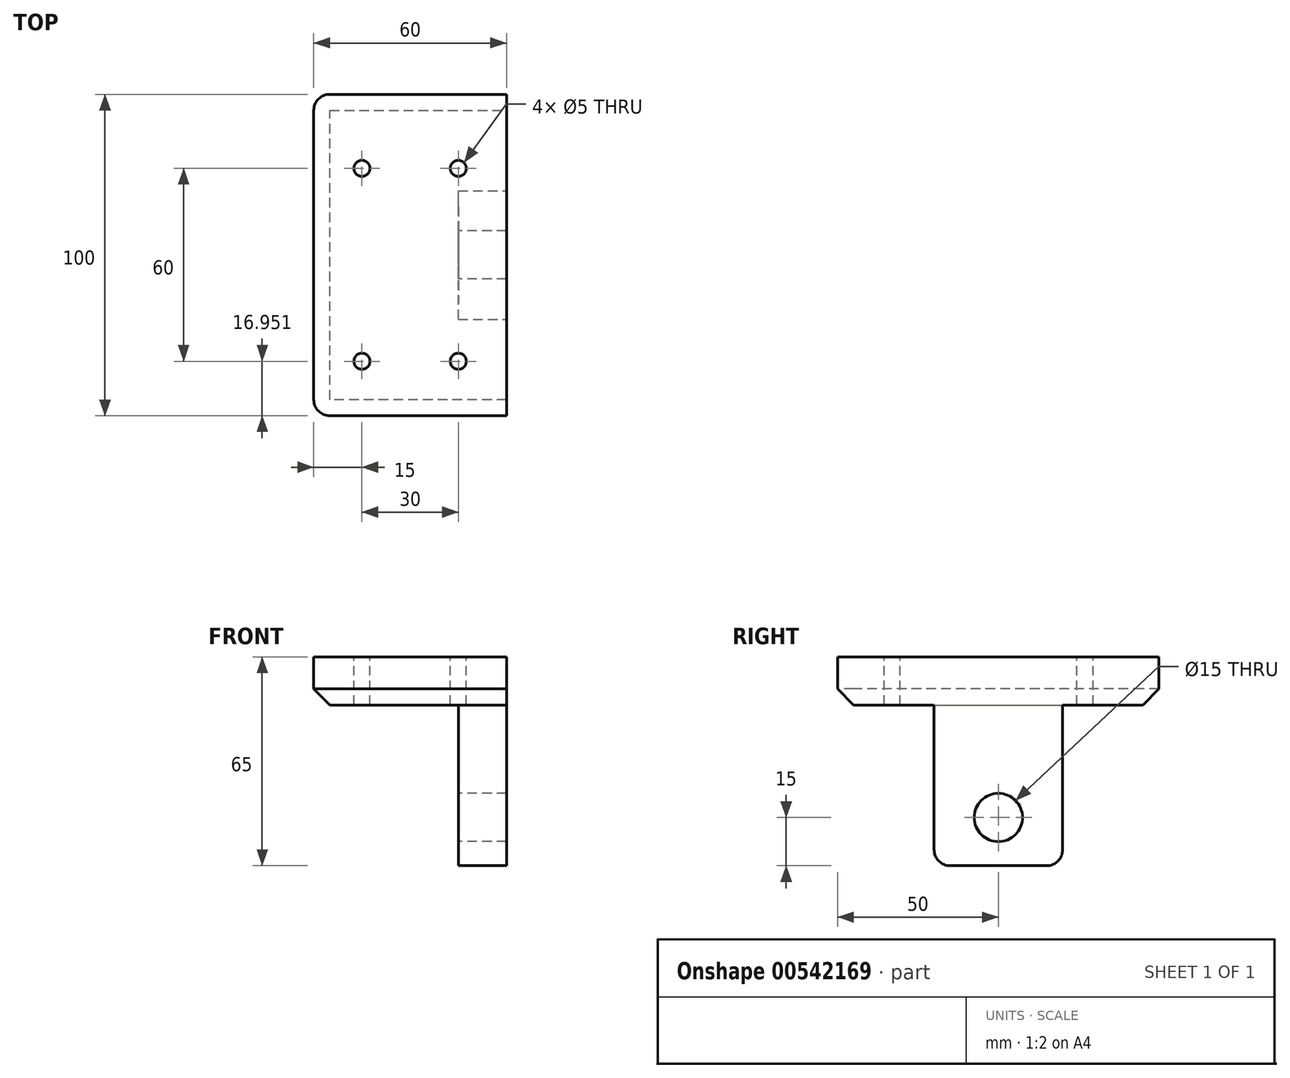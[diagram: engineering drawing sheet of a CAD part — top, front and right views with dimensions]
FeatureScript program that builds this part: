
annotation { "Feature Type Name" : "Feature", "Feature Type Description" : "" }
export const myFeature = defineFeature(function(context is Context, id is Id, definition is map)
    precondition{}
    {
        {
            var Q0;
            Q0=qCreatedBy(makeId("Top.planeOp"),FACE);
            var sketch = newSketch(context, id + "F0", { "sketchPlane" : qUnion([Q0])});
            skLineSegment(sketch, "E0.bottom", {"start": v(5, 0) * mm, "end": v(60, 0) * mm});
            skLineSegment(sketch, "E0.top", {"start": v(5, 100) * mm, "end": v(60, 100) * mm});
            skLineSegment(sketch, "E0.left", {"start": v(0, 5) * mm, "end": v(0, 95) * mm});
            skLineSegment(sketch, "E0.right", {"start": v(60, 0) * mm, "end": v(60, 100) * mm});
            skPoint(sketch, "E1.visualSharp", {"position": v(0, 100) * mm});
            skArc(sketch, "E1.filletArc", {"start": v(5, 100) * mm, "mid": v(1.46, 98.54) * mm, "end": v(0, 95) * mm});
            skPoint(sketch, "E2.visualSharp", {"position": v(0, 0) * mm});
            skArc(sketch, "E2.filletArc", {"start": v(0, 5) * mm, "mid": v(1.46, 1.46) * mm, "end": v(5, 0) * mm});
            skSolve(sketch);
        }
        {
            var Q0;
            Q0=makeQuery(id+"F0.imprint","IMPRINT",FACE,{"disambiguationData":[TD([[makeQuery(id+"F0.imprint","IMPRINT",EDGE,{"derivedFrom":sQuery(id+"F0.wireOp",EDGE,"E0.bottom")}),1.0]])]});
            extrude(context, id + "F1", {"entities" : qUnion([Q0]), "oppositeDirection" : true, "depth" : 15 * mm, "offsetDistance" : 25 * mm});
        }
        {
            var Q0;
            Q0=makeQuery(id+"F1.opExtrude","SWEPT_FACE",FACE,{"disambiguationData":[OSD([sQuery(id+"F0.wireOp",EDGE,"E0.right")])]});
            var sketch = newSketch(context, id + "F2", { "sketchPlane" : qUnion([Q0])});
            skLineSegment(sketch, "E3.bottom", {"start": v(70, -15) * mm, "end": v(30, -15) * mm});
            skLineSegment(sketch, "E3.top", {"start": v(70, -65) * mm, "end": v(30, -65) * mm});
            skLineSegment(sketch, "E3.left", {"start": v(70, -15) * mm, "end": v(70, -65) * mm});
            skLineSegment(sketch, "E3.right", {"start": v(30, -15) * mm, "end": v(30, -65) * mm});
            skSolve(sketch);
        }
        {
            var Q0;
            Q0=makeQuery(id+"F2.imprint","IMPRINT",FACE,{"disambiguationData":[TD([[makeQuery(id+"F2.imprint","IMPRINT",EDGE,{"derivedFrom":sQuery(id+"F2.wireOp",EDGE,"E3.bottom")}),-1.0]])]});
            extrude(context, id + "F3", {"entities" : qUnion([Q0]), "operationType" : NewBodyOperationType.ADD, "oppositeDirection" : true, "depth" : 15 * mm, "offsetDistance" : 25 * mm});
        }
        {
            var Q0;
            Q0=makeQuery(id+"F3.opExtrude","SWEPT_EDGE",EDGE,{"disambiguationData":[OSD([sQuery(id+"F2.wireOp",EDGE,"E3.top"),sQuery(id+"F2.wireOp",EDGE,"E3.left")])]});
            var Q1;
            Q1=makeQuery(id+"F3.opExtrude","SWEPT_EDGE",EDGE,{"disambiguationData":[OSD([sQuery(id+"F2.wireOp",EDGE,"E3.top"),sQuery(id+"F2.wireOp",EDGE,"E3.right")])]});
            var Q2;
            Q2=makeQuery(id+"F3.opExtrude","CAP_EDGE",EDGE,{"disambiguationData":[OSD([sQuery(id+"F2.wireOp",EDGE,"E3.bottom")])],"isStart":false});
            var Q3;
            Q3=makeQuery(id+"F3.opExtrude","SWEPT_EDGE",EDGE,{"disambiguationData":[OSD([sQuery(id+"F0.wireOp",EDGE,"E0.right"),sQuery(id+"F2.wireOp",EDGE,"E3.bottom"),sQuery(id+"F2.wireOp",EDGE,"E3.left")])]});
            var Q4;
            Q4=makeQuery(id+"F3.opExtrude","SWEPT_EDGE",EDGE,{"disambiguationData":[OSD([sQuery(id+"F0.wireOp",EDGE,"E0.right"),sQuery(id+"F2.wireOp",EDGE,"E3.bottom"),sQuery(id+"F2.wireOp",EDGE,"E3.right")])]});
            fillet(context, id + "F4", {"entities" : qUnion([Q0, Q1, Q2, Q3, Q4]), "radius" : 5 * mm, "tangentPropagation" : true, "allowEdgeOverflow" : false});
        }
        {
            var Q0;
            Q0=makeQuery(id+"F1.opExtrude","CAP_EDGE",EDGE,{"disambiguationData":[OSD([sQuery(id+"F0.wireOp",EDGE,"E0.top")])],"isStart":false});
            chamfer(context, id + "F5", {"entities" : qUnion([Q0]), "width" : 5 * mm, "tangentPropagation" : true});
        }
        {
            var Q0;
            Q0=makeQuery(id+"F3.opExtrude","CAP_FACE",FACE,{"disambiguationData":[OSD([sQuery(id+"F2.wireOp",EDGE,"E3.bottom"),sQuery(id+"F2.wireOp",EDGE,"E3.top"),sQuery(id+"F2.wireOp",EDGE,"E3.left"),sQuery(id+"F2.wireOp",EDGE,"E3.right")])],"isStart":false});
            var sketch = newSketch(context, id + "F6", { "sketchPlane" : qUnion([Q0])});
            skLineSegment(sketch, "E4", {"start": v(-50, -65) * mm, "end": v(-50, -20) * mm, "construction": true});
            skCircle(sketch, "E5", {"center": v(-50, -50) * mm, "radius": 7.5 * mm});
            skSolve(sketch);
        }
        {
            var Q0;
            Q0 = qSketchRegion(id + "F6", true);
            extrude(context, id + "F7", {"entities" : qUnion([Q0]), "operationType" : NewBodyOperationType.REMOVE, "oppositeDirection" : true, "depth" : 25 * mm, "offsetDistance" : 25 * mm});
        }
        {
            var Q0;
            Q0=makeQuery(id+"F1.opExtrude","CAP_FACE",FACE,{"disambiguationData":[OSD([sQuery(id+"F0.wireOp",EDGE,"E0.bottom"),sQuery(id+"F0.wireOp",EDGE,"E0.top"),sQuery(id+"F0.wireOp",EDGE,"E0.left"),sQuery(id+"F0.wireOp",EDGE,"E0.right"),sQuery(id+"F0.wireOp",EDGE,"E1.filletArc"),sQuery(id+"F0.wireOp",EDGE,"E2.filletArc")])],"isStart":true});
            var sketch = newSketch(context, id + "F8", { "sketchPlane" : qUnion([Q0])});
            skCircle(sketch, "E6", {"center": v(15, 16.95) * mm, "radius": 2.5 * mm});
            skCircle(sketch, "E7.0.1.0", {"center": v(15, 76.95) * mm, "radius": 2.5 * mm});
            skCircle(sketch, "E7.1.0.0", {"center": v(45, 16.95) * mm, "radius": 2.5 * mm});
            skCircle(sketch, "E7.1.1.0", {"center": v(45, 76.95) * mm, "radius": 2.5 * mm});
            skLineSegment(sketch, "E7.direction1", {"start": v(15, 16.95) * mm, "end": v(45, 16.95) * mm, "construction": true});
            skLineSegment(sketch, "E7.direction2", {"start": v(15, 16.95) * mm, "end": v(15, 76.95) * mm, "construction": true});
            skSolve(sketch);
        }
        {
            var Q0;
            Q0 = qSketchRegion(id + "F8", true);
            extrude(context, id + "F9", {"entities" : qUnion([Q0]), "operationType" : NewBodyOperationType.REMOVE, "oppositeDirection" : true, "depth" : 25 * mm, "offsetDistance" : 25 * mm});
        }
    });
